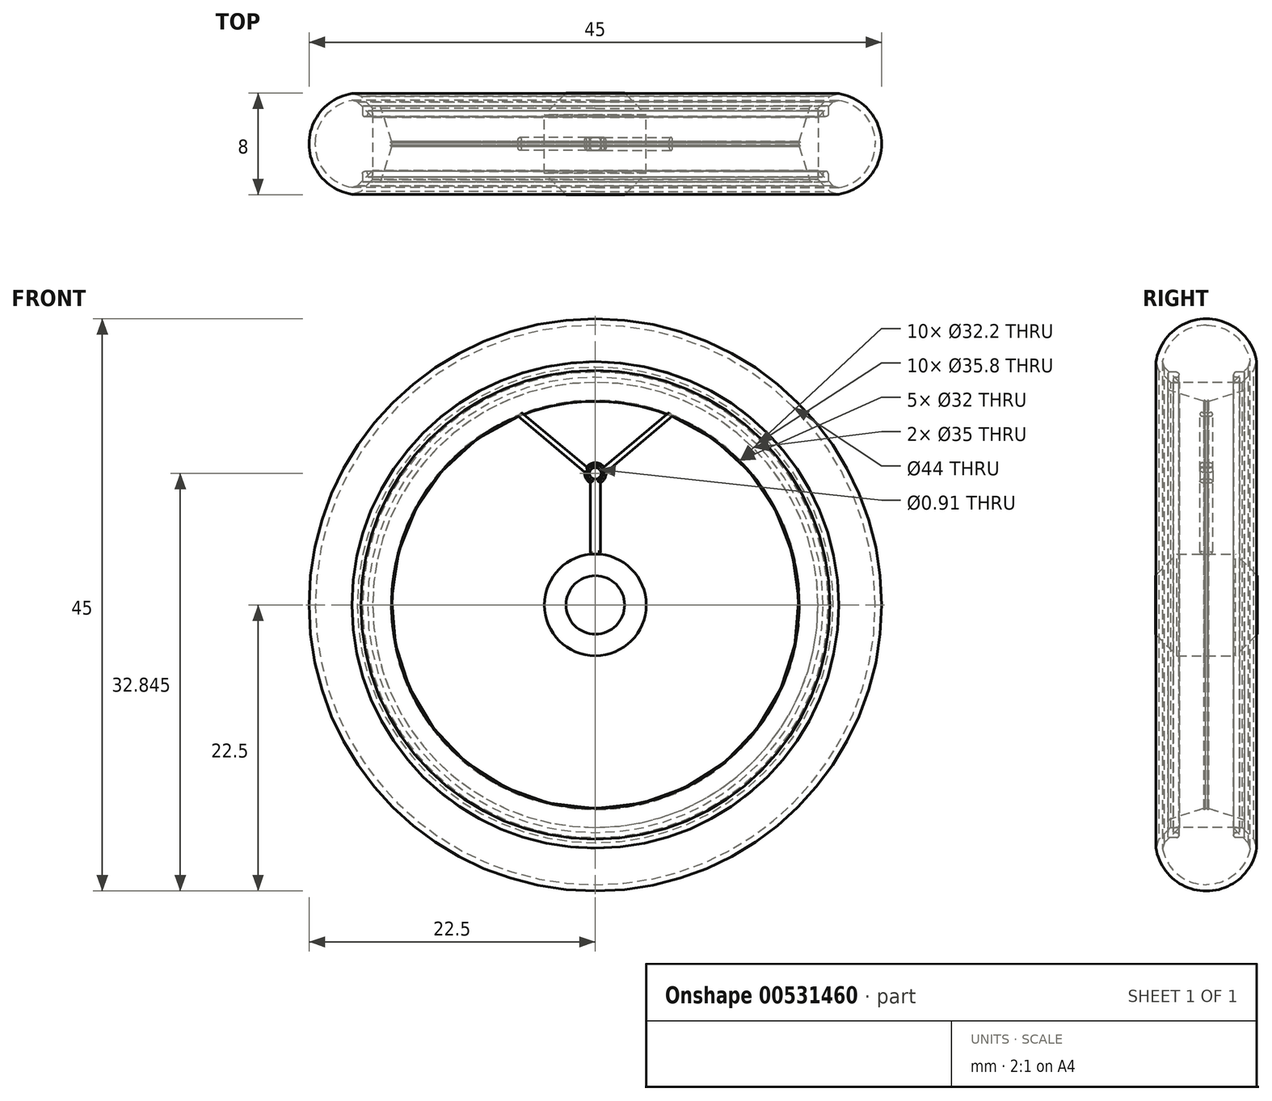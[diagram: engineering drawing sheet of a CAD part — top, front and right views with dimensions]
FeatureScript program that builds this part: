
annotation { "Feature Type Name" : "Feature", "Feature Type Description" : "" }
export const myFeature = defineFeature(function(context is Context, id is Id, definition is map)
    precondition{}
    {
        {
            var Q0;
            Q0=qCreatedBy(makeId("Front.planeOp"),FACE);
            var sketch = newSketch(context, id + "F0", { "sketchPlane" : qUnion([Q0])});
            skLineSegment(sketch, "E0", {"start": v(-60, 19.95) * mm, "end": v(-60, -19.95) * mm, "construction": true});
            skLineSegment(sketch, "E1", {"start": v(35, 21.74) * mm, "end": v(35, -21.74) * mm, "construction": true});
            skCircle(sketch, "E2", {"center": v(-60, 0) * mm, "radius": 22.5 * mm});
            skPoint(sketch, "E2.centerSnap0", {"position": v(-60, 0) * mm});
            skCircle(sketch, "E3", {"center": v(35, 0) * mm, "radius": 23 * mm});
            skPoint(sketch, "E3.centerSnap0", {"position": v(35, 0) * mm});
            skCircle(sketch, "E4", {"center": v(-60, 0) * mm, "radius": 17.5 * mm});
            skCircle(sketch, "E5", {"center": v(35, 0) * mm, "radius": 16.5 * mm});
            skSolve(sketch);
        }
        {
            var Q0;
            Q0=sQuery(id+"F0.wireOp",EDGE,"E0");
            cPlane(context, id + "F1", {"entities" : qUnion([Q0]), "cplaneType" : CPlaneType.LINE_ANGLE, "offset" : 25 * mm, "angle" : 0 * degree, "width" : 150 * mm, "height" : 150 * mm});
        }
        {
            var Q0;
            Q0=qCreatedBy(id+"F1.planeOp",FACE);
            var sketch = newSketch(context, id + "F2", { "sketchPlane" : qUnion([Q0])});
            skLineSegment(sketch, "E6", {"start": v(0, 0) * mm, "end": v(0, 39.25) * mm, "construction": true});
            skLineSegment(sketch, "E7", {"start": v(0, 17.5) * mm, "end": v(-2.4, 17.5) * mm});
            skLineSegment(sketch, "E8", {"start": v(-2.6, 17.7) * mm, "end": v(-2.6, 17.83) * mm});
            skLineSegment(sketch, "E9", {"start": v(-2.6, 17.9) * mm, "end": v(-2.6, 17.9) * mm});
            skLineSegment(sketch, "E10", {"start": v(-2.53, 17.9) * mm, "end": v(-2.35, 17.9) * mm});
            skLineSegment(sketch, "E11", {"start": v(-2.15, 18.1) * mm, "end": v(-2.15, 18.1) * mm});
            skLineSegment(sketch, "E12", {"start": v(-2.35, 18.3) * mm, "end": v(-2.93, 18.3) * mm});
            skLineSegment(sketch, "E13", {"start": v(-3, 18.23) * mm, "end": v(-3, 17.05) * mm});
            skLineSegment(sketch, "E14", {"start": v(-2.86, 16.86) * mm, "end": v(-0.22, 16.01) * mm});
            skLineSegment(sketch, "E15", {"start": v(-0.18, 16.04) * mm, "end": v(-0.18, 16.07) * mm});
            skLineSegment(sketch, "E16", {"start": v(-0.15, 16.1) * mm, "end": v(-0.13, 16.1) * mm});
            skLineSegment(sketch, "E17", {"start": v(-0.1, 16.07) * mm, "end": v(-0.1, 16.03) * mm});
            skLineSegment(sketch, "E18", {"start": v(-0.07, 16) * mm, "end": v(0, 16) * mm});
            skPoint(sketch, "E19.visualSharp", {"position": v(-2.15, 18.3) * mm});
            skArc(sketch, "E19.filletArc", {"start": v(-2.15, 18.1) * mm, "mid": v(-2.2, 18.24) * mm, "end": v(-2.35, 18.3) * mm});
            skPoint(sketch, "E20.visualSharp", {"position": v(-2.15, 17.9) * mm});
            skArc(sketch, "E20.filletArc", {"start": v(-2.35, 17.9) * mm, "mid": v(-2.2, 17.96) * mm, "end": v(-2.15, 18.1) * mm});
            skPoint(sketch, "E21.visualSharp", {"position": v(-2.6, 17.5) * mm});
            skArc(sketch, "E21.filletArc", {"start": v(-2.6, 17.7) * mm, "mid": v(-2.54, 17.56) * mm, "end": v(-2.4, 17.5) * mm});
            skPoint(sketch, "E22.visualSharp", {"position": v(-2.6, 17.9) * mm});
            skArc(sketch, "E22.filletArc", {"start": v(-2.53, 17.9) * mm, "mid": v(-2.58, 17.88) * mm, "end": v(-2.6, 17.83) * mm});
            skPoint(sketch, "E23.visualSharp", {"position": v(-3, 18.3) * mm});
            skArc(sketch, "E23.filletArc", {"start": v(-2.93, 18.3) * mm, "mid": v(-2.98, 18.28) * mm, "end": v(-3, 18.23) * mm});
            skPoint(sketch, "E24.visualSharp", {"position": v(-3, 16.9) * mm});
            skArc(sketch, "E24.filletArc", {"start": v(-3, 17.05) * mm, "mid": v(-2.96, 16.93) * mm, "end": v(-2.86, 16.86) * mm});
            skPoint(sketch, "E25.visualSharp", {"position": v(-0.1, 16) * mm});
            skArc(sketch, "E25.filletArc", {"start": v(-0.1, 16.03) * mm, "mid": v(-0.1, 16) * mm, "end": v(-0.07, 16) * mm});
            skPoint(sketch, "E26.visualSharp", {"position": v(-0.18, 16) * mm});
            skArc(sketch, "E26.filletArc", {"start": v(-0.22, 16.01) * mm, "mid": v(-0.2, 16.02) * mm, "end": v(-0.18, 16.04) * mm});
            skPoint(sketch, "E27.visualSharp", {"position": v(-0.1, 16.1) * mm});
            skArc(sketch, "E27.filletArc", {"start": v(-0.1, 16.07) * mm, "mid": v(-0.1, 16.1) * mm, "end": v(-0.13, 16.1) * mm});
            skPoint(sketch, "E28.visualSharp", {"position": v(-0.18, 16.1) * mm});
            skArc(sketch, "E28.filletArc", {"start": v(-0.15, 16.1) * mm, "mid": v(-0.17, 16.1) * mm, "end": v(-0.18, 16.07) * mm});
            skLineSegment(sketch, "E29.MirrorCS", {"start": v(0.07, 16) * mm, "end": v(0, 16) * mm});
            skArc(sketch, "E30.MirrorCS", {"start": v(0.1, 16.03) * mm, "mid": v(0.1, 16) * mm, "end": v(0.07, 16) * mm});
            skLineSegment(sketch, "E31.MirrorCS", {"start": v(0.1, 16.07) * mm, "end": v(0.1, 16.03) * mm});
            skArc(sketch, "E32.MirrorCS", {"start": v(0.1, 16.07) * mm, "mid": v(0.1, 16.1) * mm, "end": v(0.13, 16.1) * mm});
            skLineSegment(sketch, "E33.MirrorCS", {"start": v(0.15, 16.1) * mm, "end": v(0.13, 16.1) * mm});
            skArc(sketch, "E34.MirrorCS", {"start": v(0.15, 16.1) * mm, "mid": v(0.17, 16.1) * mm, "end": v(0.18, 16.07) * mm});
            skLineSegment(sketch, "E35.MirrorCS", {"start": v(0.18, 16.04) * mm, "end": v(0.18, 16.07) * mm});
            skArc(sketch, "E36.MirrorCS", {"start": v(0.22, 16.01) * mm, "mid": v(0.2, 16.02) * mm, "end": v(0.18, 16.04) * mm});
            skLineSegment(sketch, "E37.MirrorCS", {"start": v(2.86, 16.86) * mm, "end": v(0.22, 16.01) * mm});
            skArc(sketch, "E38.MirrorCS", {"start": v(3, 17.05) * mm, "mid": v(2.96, 16.93) * mm, "end": v(2.86, 16.86) * mm});
            skLineSegment(sketch, "E39.MirrorCS", {"start": v(3, 18.23) * mm, "end": v(3, 17.05) * mm});
            skPoint(sketch, "E40.MirrorP", {"position": v(3, 18.3) * mm});
            skArc(sketch, "E41.MirrorCS", {"start": v(2.93, 18.3) * mm, "mid": v(2.98, 18.28) * mm, "end": v(3, 18.23) * mm});
            skLineSegment(sketch, "E42.MirrorCS", {"start": v(2.35, 18.3) * mm, "end": v(2.93, 18.3) * mm});
            skArc(sketch, "E43.MirrorCS", {"start": v(2.15, 18.1) * mm, "mid": v(2.2, 18.24) * mm, "end": v(2.35, 18.3) * mm});
            skArc(sketch, "E44.MirrorCS", {"start": v(2.35, 17.9) * mm, "mid": v(2.2, 17.96) * mm, "end": v(2.15, 18.1) * mm});
            skLineSegment(sketch, "E45.MirrorCS", {"start": v(2.53, 17.9) * mm, "end": v(2.35, 17.9) * mm});
            skPoint(sketch, "E46.MirrorP", {"position": v(2.6, 17.9) * mm});
            skArc(sketch, "E47.MirrorCS", {"start": v(2.53, 17.9) * mm, "mid": v(2.58, 17.88) * mm, "end": v(2.6, 17.83) * mm});
            skLineSegment(sketch, "E48.MirrorCS", {"start": v(2.6, 17.7) * mm, "end": v(2.6, 17.83) * mm});
            skArc(sketch, "E49.MirrorCS", {"start": v(2.6, 17.7) * mm, "mid": v(2.54, 17.56) * mm, "end": v(2.4, 17.5) * mm});
            skLineSegment(sketch, "E50.MirrorCS", {"start": v(0, 17.5) * mm, "end": v(2.4, 17.5) * mm});
            skLineSegment(sketch, "E51", {"start": v(11.95, 0) * mm, "end": v(-11.71, 0) * mm, "construction": true});
            skSolve(sketch);
        }
        {
            var Q0;
            Q0=makeQuery(id+"F2.imprint","IMPRINT",FACE,{"disambiguationData":[TD([[makeQuery(id+"F2.imprint","IMPRINT",EDGE,{"derivedFrom":sQuery(id+"F2.wireOp",EDGE,"E7")}),1.0]])]});
            var Q1;
            Q1=sQuery(id+"F2.wireOp",EDGE,"E51");
            revolve(context, id + "F3", {"entities" : qUnion([Q0]), "axis" : qUnion([Q1]), "revolveType" : RevolveType.FULL});
        }
        {
            var Q0;
            Q0=makeQuery(id+"F0.imprint","IMPRINT",FACE,{"disambiguationData":[TD([[makeQuery(id+"F0.imprint","IMPRINT",EDGE,{"derivedFrom":sQuery(id+"F0.wireOp",EDGE,"E2")}),1.0]])]});
            extrude(context, id + "F4", {"entities" : qUnion([Q0]), "endBound" : BoundingType.SYMMETRIC, "depth" : 8 * mm, "offsetDistance" : 25 * mm});
        }
        {
            var Q0;
            Q0=makeQuery(id+"F4.opExtrude","CAP_EDGE",EDGE,{"disambiguationData":[OSD([sQuery(id+"F0.wireOp",EDGE,"E4")])],"isStart":true});
            var Q1;
            Q1=makeQuery(id+"F4.opExtrude","CAP_EDGE",EDGE,{"disambiguationData":[OSD([sQuery(id+"F0.wireOp",EDGE,"E4")])],"isStart":false});
            chamfer(context, id + "F5", {"entities" : qUnion([Q0, Q1]), "width" : 1.2 * mm, "tangentPropagation" : true});
        }
        {
            var Q0;
            Q0=makeQuery(id+"F4.opExtrude","CAP_EDGE",EDGE,{"disambiguationData":[OSD([sQuery(id+"F0.wireOp",EDGE,"E2")])],"isStart":true});
            var Q1;
            Q1=makeQuery(id+"F4.opExtrude","CAP_EDGE",EDGE,{"disambiguationData":[OSD([sQuery(id+"F0.wireOp",EDGE,"E2")])],"isStart":false});
            fillet(context, id + "F6", {"entities" : qUnion([Q0, Q1]), "radius" : 4 * mm, "tangentPropagation" : true, "allowEdgeOverflow" : false});
        }
        {
            var Q0;
            {var subQ0=sQuery(id+"F0.wireOp",EDGE,"E4");Q0=makeQuery(id+"F6.opFillet","BLEND_EDGE",EDGE,{"blendedFrom":[makeQuery(id+"F4.opExtrude","CAP_EDGE",EDGE,{"disambiguationData":[OSD([sQuery(id+"F0.wireOp",EDGE,"E2")])],"isStart":true}),makeQuery(id+"F5.opChamfer","BLEND_FACE",FACE,{"disambiguationData":[OSD([subQ0]),TDD([makeQuery(id+"F4.opExtrude","CAP_EDGE",EDGE,{"disambiguationData":[OSD([subQ0])],"isStart":true})])]})],"blendedInto":[makeQuery(id+"F5.opChamfer","BLEND_FACE",FACE,{"disambiguationData":[OSD([subQ0]),TDD([makeQuery(id+"F4.opExtrude","CAP_EDGE",EDGE,{"disambiguationData":[OSD([subQ0])],"isStart":true})])]})]});}
            var Q1;
            {var subQ0=sQuery(id+"F0.wireOp",EDGE,"E4");Q1=makeQuery(id+"F6.opFillet","BLEND_EDGE",EDGE,{"blendedFrom":[makeQuery(id+"F4.opExtrude","CAP_EDGE",EDGE,{"disambiguationData":[OSD([sQuery(id+"F0.wireOp",EDGE,"E2")])],"isStart":false}),makeQuery(id+"F5.opChamfer","BLEND_FACE",FACE,{"disambiguationData":[OSD([subQ0]),TDD([makeQuery(id+"F4.opExtrude","CAP_EDGE",EDGE,{"disambiguationData":[OSD([subQ0])],"isStart":false})])]})],"blendedInto":[makeQuery(id+"F5.opChamfer","BLEND_FACE",FACE,{"disambiguationData":[OSD([subQ0]),TDD([makeQuery(id+"F4.opExtrude","CAP_EDGE",EDGE,{"disambiguationData":[OSD([subQ0])],"isStart":false})])]})]});}
            chamfer(context, id + "F7", {"entities" : qUnion([Q0, Q1]), "width" : 0.8 * mm, "tangentPropagation" : true});
        }
        {
            var Q0;
            Q0=makeQuery(id+"F4.opExtrude","SWEPT_FACE",FACE,{"disambiguationData":[OSD([sQuery(id+"F0.wireOp",EDGE,"E4")])]});
            shell(context, id + "F8", {"entities" : qUnion([Q0]), "thickness" : 0.5 * mm});
        }
        {
            var Q0;
            Q0=qCreatedBy(makeId("Front.planeOp"),FACE);
            var sketch = newSketch(context, id + "F9", { "sketchPlane" : qUnion([Q0])});
            skLineSegment(sketch, "E52", {"start": v(-126.83, 0) * mm, "end": v(-126.83, 0) * mm});
            skLineSegment(sketch, "E53", {"start": v(-60, 20.43) * mm, "end": v(-60, -22.96) * mm, "construction": true});
            skCircle(sketch, "E54", {"center": v(-60, 0) * mm, "radius": 4 * mm});
            skLineSegment(sketch, "E55", {"start": v(-59.6, 3.98) * mm, "end": v(-59.6, 9.6) * mm});
            skLineSegment(sketch, "E56", {"start": v(-59.17, 10.45) * mm, "end": v(-53.93, 14.84) * mm});
            skLineSegment(sketch, "E57", {"start": v(-59.32, 10.84) * mm, "end": v(-54.19, 15.15) * mm});
            skLineSegment(sketch, "E58", {"start": v(-54.19, 15.15) * mm, "end": v(-53.93, 14.84) * mm});
            skLineSegment(sketch, "E59.MirrorCS", {"start": v(-60.4, 3.98) * mm, "end": v(-60.4, 9.6) * mm});
            skLineSegment(sketch, "E60.MirrorCS", {"start": v(-60.83, 10.45) * mm, "end": v(-66.07, 14.84) * mm});
            skLineSegment(sketch, "E61.MirrorCS", {"start": v(-60.68, 10.84) * mm, "end": v(-65.81, 15.15) * mm});
            skLineSegment(sketch, "E62.MirrorCS", {"start": v(-65.81, 15.15) * mm, "end": v(-66.07, 14.84) * mm});
            skArc(sketch, "E63", {"start": v(-60.83, 10.45) * mm, "mid": v(-60.75, 9.96) * mm, "end": v(-60.4, 9.6) * mm});
            skCircle(sketch, "E64", {"center": v(-60, 10.35) * mm, "radius": 0.46 * mm});
            skPoint(sketch, "E65.orphan", {"position": v(-60.4, 10.6) * mm});
            skPoint(sketch, "E66.orphan", {"position": v(-60.4, 10.09) * mm});
            skArc(sketch, "E67.trimOffspring", {"start": v(-59.6, 9.6) * mm, "mid": v(-59.25, 9.96) * mm, "end": v(-59.17, 10.45) * mm});
            skPoint(sketch, "E68.orphan", {"position": v(-59.6, 10.6) * mm});
            skArc(sketch, "E69.trimOffspring", {"start": v(-59.32, 10.84) * mm, "mid": v(-60, 11.19) * mm, "end": v(-60.68, 10.84) * mm});
            skPoint(sketch, "E70.orphan", {"position": v(-59.6, 10.09) * mm});
            skSolve(sketch);
        }
        {
            var Q0;
            {var subQ0=sQuery(id+"F9.wireOp",EDGE,"E54");var subQ1=makeQuery(id+"F9.imprint","INTERSECT",VERTEX,{"derivedFrom":[subQ0,sQuery(id+"F9.wireOp",EDGE,"E55")]});Q0=makeQuery(id+"F9.imprint","IMPRINT",FACE,{"disambiguationData":[TD([[makeQuery(id+"F9.imprint","IMPRINT",EDGE,{"disambiguationData":[TD([[subQ1,-1.0]])],"derivedFrom":subQ0}),1.0]])]});}
            extrude(context, id + "F10", {"entities" : qUnion([Q0]), "endBound" : BoundingType.SYMMETRIC, "depth" : 8 * mm, "offsetDistance" : 25 * mm});
        }
        {
            var Q0;
            Q0=makeQuery(id+"F10.opExtrude","CAP_EDGE",EDGE,{"disambiguationData":[OSD([sQuery(id+"F9.wireOp",EDGE,"E54")])],"isStart":false});
            var Q1;
            Q1=makeQuery(id+"F10.opExtrude","CAP_EDGE",EDGE,{"disambiguationData":[OSD([sQuery(id+"F9.wireOp",EDGE,"E54")])],"isStart":true});
            chamfer(context, id + "F11", {"entities" : qUnion([Q0, Q1]), "width" : 1.7 * mm, "tangentPropagation" : true});
        }
        {
            var Q0;
            {var subQ1=sQuery(id+"F9.wireOp",EDGE,"E55");Q0=makeQuery(id+"F9.imprint","IMPRINT",FACE,{"disambiguationData":[TD([[makeQuery(id+"F9.imprint","IMPRINT",EDGE,{"derivedFrom":subQ1}),1.0]])]});}
            extrude(context, id + "F12", {"entities" : qUnion([Q0]), "endBound" : BoundingType.SYMMETRIC, "depth" : 1 * mm, "offsetDistance" : 25 * mm});
        }
        {
            var Q0;
            Q0=makeQuery(id+"F12.opExtrude","CAP_EDGE",EDGE,{"disambiguationData":[OSD([sQuery(id+"F9.wireOp",EDGE,"E57")])],"isStart":true});
            var Q1;
            Q1=makeQuery(id+"F12.opExtrude","CAP_EDGE",EDGE,{"disambiguationData":[OSD([sQuery(id+"F9.wireOp",EDGE,"E57")])],"isStart":false});
            var Q2;
            Q2=makeQuery(id+"F12.opExtrude","CAP_EDGE",EDGE,{"disambiguationData":[OSD([sQuery(id+"F9.wireOp",EDGE,"E61.MirrorCS")])],"isStart":false});
            var Q3;
            Q3=makeQuery(id+"F12.opExtrude","CAP_EDGE",EDGE,{"disambiguationData":[OSD([sQuery(id+"F9.wireOp",EDGE,"E60.MirrorCS")])],"isStart":true});
            var Q4;
            Q4=makeQuery(id+"F12.opExtrude","CAP_EDGE",EDGE,{"disambiguationData":[OSD([sQuery(id+"F9.wireOp",EDGE,"E60.MirrorCS")])],"isStart":false});
            var Q5;
            Q5=makeQuery(id+"F12.opExtrude","CAP_EDGE",EDGE,{"disambiguationData":[OSD([sQuery(id+"F9.wireOp",EDGE,"E59.MirrorCS")])],"isStart":true});
            var Q6;
            Q6=makeQuery(id+"F12.opExtrude","CAP_EDGE",EDGE,{"disambiguationData":[OSD([sQuery(id+"F9.wireOp",EDGE,"E59.MirrorCS")])],"isStart":false});
            var Q7;
            Q7=makeQuery(id+"F12.opExtrude","CAP_EDGE",EDGE,{"disambiguationData":[OSD([sQuery(id+"F9.wireOp",EDGE,"E55")])],"isStart":false});
            var Q8;
            Q8=makeQuery(id+"F12.opExtrude","CAP_EDGE",EDGE,{"disambiguationData":[OSD([sQuery(id+"F9.wireOp",EDGE,"E56")])],"isStart":false});
            var Q9;
            Q9=makeQuery(id+"F12.opExtrude","CAP_EDGE",EDGE,{"disambiguationData":[OSD([sQuery(id+"F9.wireOp",EDGE,"E61.MirrorCS")])],"isStart":true});
            var Q10;
            Q10=makeQuery(id+"F12.opExtrude","CAP_EDGE",EDGE,{"disambiguationData":[OSD([sQuery(id+"F9.wireOp",EDGE,"E55")])],"isStart":true});
            var Q11;
            Q11=makeQuery(id+"F12.opExtrude","CAP_EDGE",EDGE,{"disambiguationData":[OSD([sQuery(id+"F9.wireOp",EDGE,"E56")])],"isStart":true});
            var Q12;
            Q12=makeQuery(id+"F12.opExtrude","CAP_EDGE",EDGE,{"disambiguationData":[OSD([sQuery(id+"F9.wireOp",EDGE,"E67.trimOffspring")])],"isStart":false});
            var Q13;
            Q13=makeQuery(id+"F12.opExtrude","CAP_EDGE",EDGE,{"disambiguationData":[OSD([sQuery(id+"F9.wireOp",EDGE,"E63")])],"isStart":false});
            var Q14;
            Q14=makeQuery(id+"F12.opExtrude","CAP_EDGE",EDGE,{"disambiguationData":[OSD([sQuery(id+"F9.wireOp",EDGE,"E69.trimOffspring")])],"isStart":false});
            var Q15;
            Q15=makeQuery(id+"F12.opExtrude","CAP_EDGE",EDGE,{"disambiguationData":[OSD([sQuery(id+"F9.wireOp",EDGE,"E69.trimOffspring")])],"isStart":true});
            var Q16;
            Q16=makeQuery(id+"F12.opExtrude","CAP_EDGE",EDGE,{"disambiguationData":[OSD([sQuery(id+"F9.wireOp",EDGE,"E67.trimOffspring")])],"isStart":true});
            var Q17;
            Q17=makeQuery(id+"F12.opExtrude","CAP_EDGE",EDGE,{"disambiguationData":[OSD([sQuery(id+"F9.wireOp",EDGE,"E63")])],"isStart":true});
            var Q18;
            Q18=makeQuery(id+"F12.opExtrude","CAP_EDGE",EDGE,{"disambiguationData":[OSD([sQuery(id+"F9.wireOp",EDGE,"E64")])],"isStart":false});
            var Q19;
            Q19=makeQuery(id+"F12.opExtrude","CAP_EDGE",EDGE,{"disambiguationData":[OSD([sQuery(id+"F9.wireOp",EDGE,"E64")])],"isStart":true});
            fillet(context, id + "F13", {"entities" : qUnion([Q0, Q1, Q2, Q3, Q4, Q5, Q6, Q7, Q8, Q9, Q10, Q11, Q12, Q13, Q14, Q15, Q16, Q17, Q18, Q19]), "radius" : 0.2 * mm, "tangentPropagation" : true, "allowEdgeOverflow" : false});
        }
        {
            var Q0;
            Q0=makeQuery(id+"F12.opExtrude","SWEPT_EDGE",EDGE,{"disambiguationData":[OSD([sQuery(id+"F9.wireOp",EDGE,"E54"),sQuery(id+"F9.wireOp",EDGE,"E55")])]});
            fillet(context, id + "F14", {"entities" : qUnion([Q0]), "radius" : 0.2 * mm, "tangentPropagation" : true, "allowEdgeOverflow" : false});
        }
        {
            var Q0;
            Q0=makeQuery(id+"F3.opRevolve","SWEPT_BODY",BODY,{"disambiguationData":[OSD([sQuery(id+"F2.wireOp",EDGE,"E7"),sQuery(id+"F2.wireOp",EDGE,"E8"),sQuery(id+"F2.wireOp",EDGE,"E10"),sQuery(id+"F2.wireOp",EDGE,"E12"),sQuery(id+"F2.wireOp",EDGE,"E13"),sQuery(id+"F2.wireOp",EDGE,"E14"),sQuery(id+"F2.wireOp",EDGE,"E15"),sQuery(id+"F2.wireOp",EDGE,"E16"),sQuery(id+"F2.wireOp",EDGE,"E17"),sQuery(id+"F2.wireOp",EDGE,"E18"),sQuery(id+"F2.wireOp",EDGE,"E19.filletArc"),sQuery(id+"F2.wireOp",EDGE,"E20.filletArc"),sQuery(id+"F2.wireOp",EDGE,"E21.filletArc"),sQuery(id+"F2.wireOp",EDGE,"E22.filletArc"),sQuery(id+"F2.wireOp",EDGE,"E23.filletArc"),sQuery(id+"F2.wireOp",EDGE,"E24.filletArc"),sQuery(id+"F2.wireOp",EDGE,"E25.filletArc"),sQuery(id+"F2.wireOp",EDGE,"E26.filletArc"),sQuery(id+"F2.wireOp",EDGE,"E27.filletArc"),sQuery(id+"F2.wireOp",EDGE,"E28.filletArc"),sQuery(id+"F2.wireOp",EDGE,"E29.MirrorCS"),sQuery(id+"F2.wireOp",EDGE,"E30.MirrorCS"),sQuery(id+"F2.wireOp",EDGE,"E31.MirrorCS"),sQuery(id+"F2.wireOp",EDGE,"E32.MirrorCS"),sQuery(id+"F2.wireOp",EDGE,"E33.MirrorCS"),sQuery(id+"F2.wireOp",EDGE,"E34.MirrorCS"),sQuery(id+"F2.wireOp",EDGE,"E35.MirrorCS"),sQuery(id+"F2.wireOp",EDGE,"E36.MirrorCS"),sQuery(id+"F2.wireOp",EDGE,"E37.MirrorCS"),sQuery(id+"F2.wireOp",EDGE,"E38.MirrorCS"),sQuery(id+"F2.wireOp",EDGE,"E39.MirrorCS"),sQuery(id+"F2.wireOp",EDGE,"E41.MirrorCS"),sQuery(id+"F2.wireOp",EDGE,"E42.MirrorCS"),sQuery(id+"F2.wireOp",EDGE,"E43.MirrorCS"),sQuery(id+"F2.wireOp",EDGE,"E44.MirrorCS"),sQuery(id+"F2.wireOp",EDGE,"E45.MirrorCS"),sQuery(id+"F2.wireOp",EDGE,"E47.MirrorCS"),sQuery(id+"F2.wireOp",EDGE,"E48.MirrorCS"),sQuery(id+"F2.wireOp",EDGE,"E49.MirrorCS"),sQuery(id+"F2.wireOp",EDGE,"E50.MirrorCS")])]});
            var Q1;
            {var subQ0=sQuery(id+"F9.wireOp",EDGE,"E54");Q1=makeQuery(id+"F11.opChamfer","BLEND_EDGE",EDGE,{"blendedFrom":[makeQuery(id+"F10.opExtrude","CAP_EDGE",EDGE,{"disambiguationData":[OSD([subQ0])],"isStart":false}),makeQuery(id+"F10.opExtrude","SWEPT_FACE",FACE,{"disambiguationData":[OSD([subQ0])]})],"blendedInto":[makeQuery(id+"F10.opExtrude","SWEPT_FACE",FACE,{"disambiguationData":[OSD([subQ0])]})]});}
            circularPattern(context, id + "F15", {"entities" : qUnion([Q0]), "axis" : qUnion([Q1]), "angle" : 360 * degree, "instanceCount" : 5, "equalSpace" : true});
        }
    });
